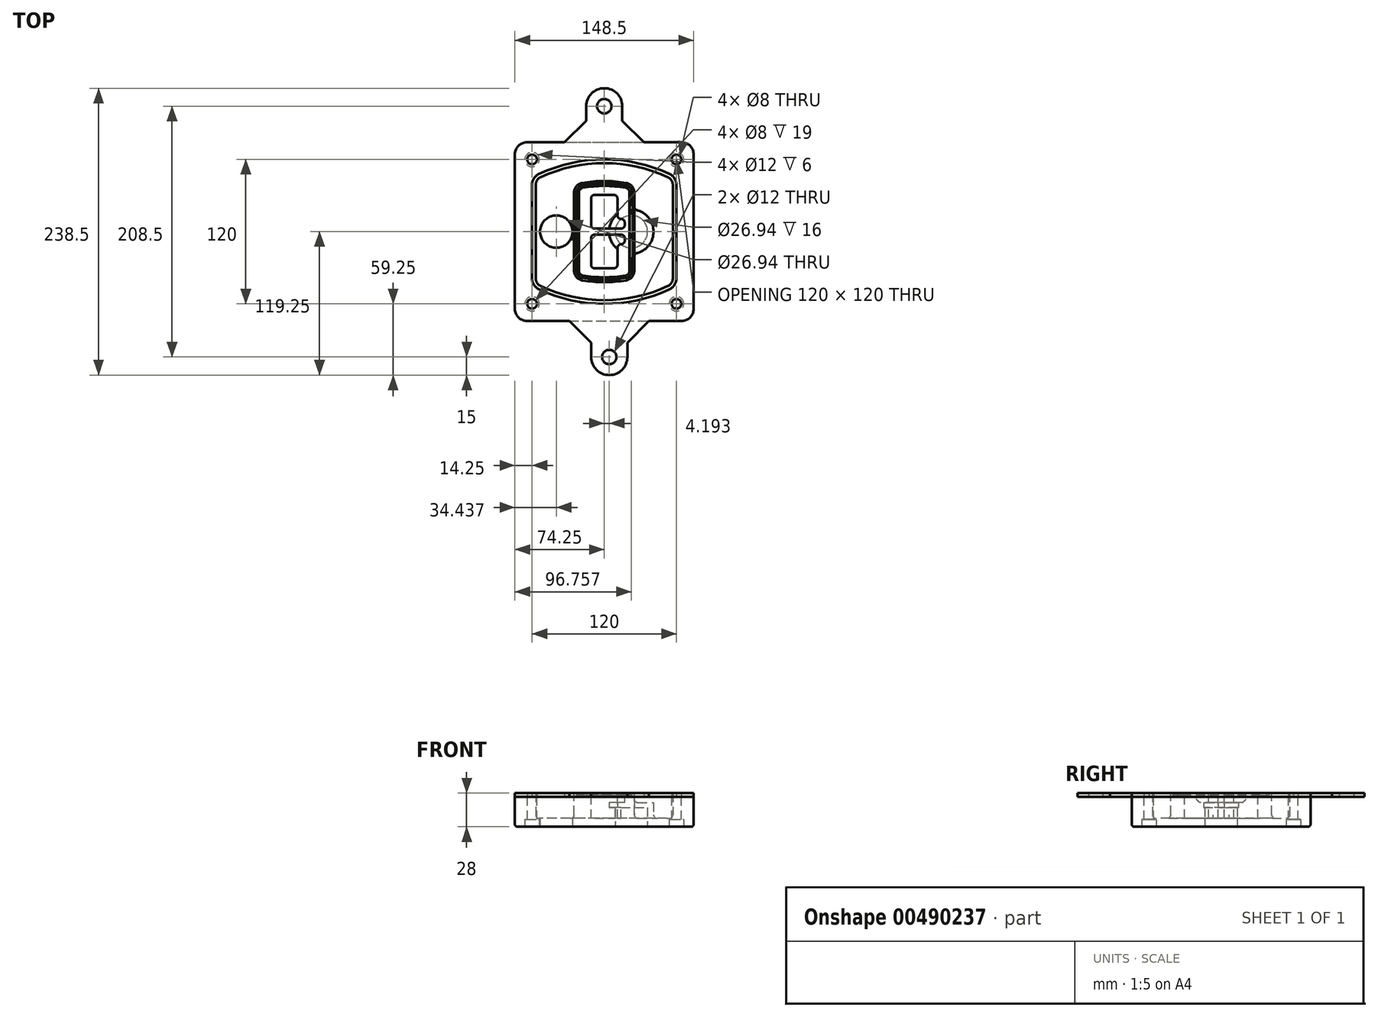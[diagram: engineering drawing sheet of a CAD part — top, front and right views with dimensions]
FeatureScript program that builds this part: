
annotation { "Feature Type Name" : "Feature", "Feature Type Description" : "" }
export const myFeature = defineFeature(function(context is Context, id is Id, definition is map)
    precondition{}
    {
        {
            var Q0;
            Q0=qCreatedBy(makeId("Top.planeOp"),FACE);
            var sketch = newSketch(context, id + "F0", { "sketchPlane" : qUnion([Q0])});
            skPoint(sketch, "E0.rect.middle", {"position": v(0, 0) * mm});
            skLineSegment(sketch, "E1.bottom", {"start": v(-64.25, -74.25) * mm, "end": v(64.25, -74.25) * mm});
            skLineSegment(sketch, "E1.top", {"start": v(-64.25, 74.25) * mm, "end": v(64.25, 74.25) * mm});
            skLineSegment(sketch, "E1.left", {"start": v(-74.25, -64.25) * mm, "end": v(-74.25, 64.25) * mm});
            skLineSegment(sketch, "E1.right", {"start": v(74.25, -64.25) * mm, "end": v(74.25, 64.25) * mm});
            skLineSegment(sketch, "E2", {"start": v(-74.25, 74.25) * mm, "end": v(74.25, -74.25) * mm, "construction": true});
            skLineSegment(sketch, "E3", {"start": v(74.25, 74.25) * mm, "end": v(-74.25, -74.25) * mm, "construction": true});
            skCircle(sketch, "E4", {"center": v(-60, 60) * mm, "radius": 4 * mm});
            skCircle(sketch, "E5", {"center": v(60, 60) * mm, "radius": 4 * mm});
            skCircle(sketch, "E6", {"center": v(60, -60) * mm, "radius": 4 * mm});
            skCircle(sketch, "E7", {"center": v(-60, -60) * mm, "radius": 4 * mm});
            skLineSegment(sketch, "E8", {"start": v(-60, 60) * mm, "end": v(60, 60) * mm, "construction": true});
            skLineSegment(sketch, "E9", {"start": v(60, 60) * mm, "end": v(60, -60) * mm, "construction": true});
            skLineSegment(sketch, "E10", {"start": v(60, -60) * mm, "end": v(-60, -60) * mm, "construction": true});
            skLineSegment(sketch, "E11", {"start": v(-60, -60) * mm, "end": v(-60, 60) * mm, "construction": true});
            skLineSegment(sketch, "E12", {"start": v(-60, 38.83) * mm, "end": v(-60, -38.83) * mm});
            skLineSegment(sketch, "E13", {"start": v(60, 38.83) * mm, "end": v(60, -38.83) * mm});
            skArc(sketch, "E14", {"start": v(54.26, 47.88) * mm, "mid": v(0, 60) * mm, "end": v(-54.26, 47.88) * mm});
            skArc(sketch, "E15", {"start": v(-54.26, -47.88) * mm, "mid": v(0, -60) * mm, "end": v(54.26, -47.88) * mm});
            skLineSegment(sketch, "E16", {"start": v(-60, 0) * mm, "end": v(60, 0) * mm, "construction": true});
            skPoint(sketch, "E17.visualSharp", {"position": v(-60, -45) * mm});
            skArc(sketch, "E17.filletArc", {"start": v(-60, -38.83) * mm, "mid": v(-58.44, -44.2) * mm, "end": v(-54.26, -47.88) * mm});
            skPoint(sketch, "E18.visualSharp", {"position": v(-60, 45) * mm});
            skArc(sketch, "E18.filletArc", {"start": v(-54.26, 47.88) * mm, "mid": v(-58.44, 44.2) * mm, "end": v(-60, 38.83) * mm});
            skPoint(sketch, "E19.visualSharp", {"position": v(60, 45) * mm});
            skArc(sketch, "E19.filletArc", {"start": v(60, 38.83) * mm, "mid": v(58.44, 44.2) * mm, "end": v(54.26, 47.88) * mm});
            skPoint(sketch, "E20.visualSharp", {"position": v(60, -45) * mm});
            skArc(sketch, "E20.filletArc", {"start": v(54.26, -47.88) * mm, "mid": v(58.44, -44.2) * mm, "end": v(60, -38.83) * mm});
            skPoint(sketch, "E21.visualSharp", {"position": v(-74.25, 74.25) * mm});
            skArc(sketch, "E21.filletArc", {"start": v(-64.25, 74.25) * mm, "mid": v(-71.32, 71.32) * mm, "end": v(-74.25, 64.25) * mm});
            skPoint(sketch, "E22.visualSharp", {"position": v(74.25, 74.25) * mm});
            skArc(sketch, "E22.filletArc", {"start": v(74.25, 64.25) * mm, "mid": v(71.32, 71.32) * mm, "end": v(64.25, 74.25) * mm});
            skPoint(sketch, "E23.visualSharp", {"position": v(74.25, -74.25) * mm});
            skArc(sketch, "E23.filletArc", {"start": v(64.25, -74.25) * mm, "mid": v(71.32, -71.32) * mm, "end": v(74.25, -64.25) * mm});
            skPoint(sketch, "E24.visualSharp", {"position": v(-74.25, -74.25) * mm});
            skArc(sketch, "E24.filletArc", {"start": v(-74.25, -64.25) * mm, "mid": v(-71.32, -71.32) * mm, "end": v(-64.25, -74.25) * mm});
            skArc(sketch, "E25.0", {"start": v(57, 38.83) * mm, "mid": v(55.9, 42.58) * mm, "end": v(52.98, 45.17) * mm});
            skLineSegment(sketch, "E25.1", {"start": v(57, 38.83) * mm, "end": v(57, -38.83) * mm});
            skArc(sketch, "E25.2", {"start": v(52.98, -45.17) * mm, "mid": v(55.9, -42.58) * mm, "end": v(57, -38.83) * mm});
            skArc(sketch, "E25.3", {"start": v(-52.98, -45.17) * mm, "mid": v(0, -57) * mm, "end": v(52.98, -45.17) * mm});
            skArc(sketch, "E25.4", {"start": v(-57, -38.83) * mm, "mid": v(-55.9, -42.58) * mm, "end": v(-52.98, -45.17) * mm});
            skArc(sketch, "E25.5", {"start": v(52.98, 45.17) * mm, "mid": v(0, 57) * mm, "end": v(-52.98, 45.17) * mm});
            skLineSegment(sketch, "E25.6", {"start": v(-57, 38.83) * mm, "end": v(-57, -38.83) * mm});
            skArc(sketch, "E25.7", {"start": v(-52.98, 45.17) * mm, "mid": v(-55.9, 42.58) * mm, "end": v(-57, 38.83) * mm});
            skArc(sketch, "E26.0", {"start": v(-55.96, 51.5) * mm, "mid": v(-61.82, 46.33) * mm, "end": v(-64, 38.83) * mm});
            skArc(sketch, "E26.1", {"start": v(55.96, 51.5) * mm, "mid": v(0, 64) * mm, "end": v(-55.96, 51.5) * mm});
            skArc(sketch, "E26.2", {"start": v(64, 38.83) * mm, "mid": v(61.82, 46.33) * mm, "end": v(55.96, 51.5) * mm});
            skLineSegment(sketch, "E26.3", {"start": v(64, 38.83) * mm, "end": v(64, -38.83) * mm});
            skArc(sketch, "E26.4", {"start": v(55.96, -51.5) * mm, "mid": v(61.82, -46.33) * mm, "end": v(64, -38.83) * mm});
            skLineSegment(sketch, "E26.5", {"start": v(-64, 38.83) * mm, "end": v(-64, -38.83) * mm});
            skArc(sketch, "E26.6", {"start": v(-55.96, -51.5) * mm, "mid": v(0, -64) * mm, "end": v(55.96, -51.5) * mm});
            skArc(sketch, "E26.7", {"start": v(-64, -38.83) * mm, "mid": v(-61.82, -46.33) * mm, "end": v(-55.96, -51.5) * mm});
            skSolve(sketch);
        }
        {
            var Q0;
            Q0=makeQuery(id+"F0.imprint","IMPRINT",FACE,{"disambiguationData":[TD([[makeQuery(id+"F0.imprint","IMPRINT",EDGE,{"derivedFrom":sQuery(id+"F0.wireOp",EDGE,"E1.bottom")}),1.0]])]});
            var Q1;
            Q1=makeQuery(id+"F0.imprint","IMPRINT",FACE,{"disambiguationData":[TD([[makeQuery(id+"F0.imprint","IMPRINT",EDGE,{"derivedFrom":sQuery(id+"F0.wireOp",EDGE,"E12")}),1.0]])]});
            var Q2;
            Q2=makeQuery(id+"F0.imprint","IMPRINT",FACE,{"disambiguationData":[TD([[makeQuery(id+"F0.imprint","IMPRINT",EDGE,{"derivedFrom":sQuery(id+"F0.wireOp",EDGE,"E25.0")}),1.0]])]});
            var Q3;
            Q3=makeQuery(id+"F0.imprint","IMPRINT",FACE,{"disambiguationData":[TD([[makeQuery(id+"F0.imprint","IMPRINT",EDGE,{"derivedFrom":sQuery(id+"F0.wireOp",EDGE,"E12")}),-1.0]])]});
            extrude(context, id + "F1", {"entities" : qUnion([Q0, Q1, Q2, Q3]), "oppositeDirection" : true, "depth" : 25 * mm});
        }
        {
            var Q0;
            Q0=makeQuery(id+"F0.imprint","IMPRINT",FACE,{"disambiguationData":[TD([[makeQuery(id+"F0.imprint","IMPRINT",EDGE,{"derivedFrom":sQuery(id+"F0.wireOp",EDGE,"E12")}),1.0]])]});
            extrude(context, id + "F2", {"entities" : qUnion([Q0]), "operationType" : NewBodyOperationType.ADD, "depth" : 3 * mm});
        }
        {
            var Q0;
            Q0=makeQuery(id+"F0.imprint","IMPRINT",FACE,{"disambiguationData":[TD([[makeQuery(id+"F0.imprint","IMPRINT",EDGE,{"derivedFrom":sQuery(id+"F0.wireOp",EDGE,"E25.0")}),1.0]])]});
            extrude(context, id + "F3", {"entities" : qUnion([Q0]), "operationType" : NewBodyOperationType.REMOVE, "oppositeDirection" : true, "depth" : 18 * mm});
        }
        {
            var Q0;
            Q0=makeQuery(id+"F2.opExtrude","CAP_FACE",FACE,{"disambiguationData":[OSD([sQuery(id+"F0.wireOp",EDGE,"E12"),sQuery(id+"F0.wireOp",EDGE,"E13"),sQuery(id+"F0.wireOp",EDGE,"E14"),sQuery(id+"F0.wireOp",EDGE,"E15"),sQuery(id+"F0.wireOp",EDGE,"E17.filletArc"),sQuery(id+"F0.wireOp",EDGE,"E18.filletArc"),sQuery(id+"F0.wireOp",EDGE,"E19.filletArc"),sQuery(id+"F0.wireOp",EDGE,"E20.filletArc"),sQuery(id+"F0.wireOp",EDGE,"E25.0"),sQuery(id+"F0.wireOp",EDGE,"E25.1"),sQuery(id+"F0.wireOp",EDGE,"E25.2"),sQuery(id+"F0.wireOp",EDGE,"E25.3"),sQuery(id+"F0.wireOp",EDGE,"E25.4"),sQuery(id+"F0.wireOp",EDGE,"E25.5"),sQuery(id+"F0.wireOp",EDGE,"E25.6"),sQuery(id+"F0.wireOp",EDGE,"E25.7")])],"isStart":false});
            var sketch = newSketch(context, id + "F4", { "sketchPlane" : qUnion([Q0])});
            skArc(sketch, "E27.0", {"start": v(-18.34, -40.45) * mm, "mid": v(0, -42) * mm, "end": v(18.34, -40.45) * mm});
            skArc(sketch, "E28.0", {"start": v(18.34, 40.45) * mm, "mid": v(0, 42) * mm, "end": v(-18.34, 40.45) * mm});
            skLineSegment(sketch, "E29", {"start": v(-25, 32.57) * mm, "end": v(-25, -32.57) * mm});
            skLineSegment(sketch, "E30", {"start": v(25, 32.57) * mm, "end": v(25, -32.57) * mm});
            skLineSegment(sketch, "E31", {"start": v(-25, 39.1) * mm, "end": v(25, 39.1) * mm, "construction": true});
            skLineSegment(sketch, "E32", {"start": v(-25, -39.1) * mm, "end": v(25, -39.1) * mm, "construction": true});
            skPoint(sketch, "E33.visualSharp", {"position": v(-25, 39.1) * mm});
            skArc(sketch, "E33.filletArc", {"start": v(-18.34, 40.45) * mm, "mid": v(-23.11, 37.73) * mm, "end": v(-25, 32.57) * mm});
            skPoint(sketch, "E34.visualSharp", {"position": v(25, 39.1) * mm});
            skArc(sketch, "E34.filletArc", {"start": v(25, 32.57) * mm, "mid": v(23.11, 37.73) * mm, "end": v(18.34, 40.45) * mm});
            skPoint(sketch, "E35.visualSharp", {"position": v(25, -39.1) * mm});
            skArc(sketch, "E35.filletArc", {"start": v(18.34, -40.45) * mm, "mid": v(23.11, -37.73) * mm, "end": v(25, -32.57) * mm});
            skPoint(sketch, "E36.visualSharp", {"position": v(-25, -39.1) * mm});
            skArc(sketch, "E36.filletArc", {"start": v(-25, -32.57) * mm, "mid": v(-23.11, -37.73) * mm, "end": v(-18.34, -40.45) * mm});
            skArc(sketch, "E37.0", {"start": v(52.98, 45.17) * mm, "mid": v(0, 57) * mm, "end": v(-52.98, 45.17) * mm});
            skArc(sketch, "E37.1", {"start": v(-52.98, 45.17) * mm, "mid": v(-55.9, 42.58) * mm, "end": v(-57, 38.83) * mm});
            skLineSegment(sketch, "E37.2", {"start": v(-57, 38.83) * mm, "end": v(-57, -38.83) * mm});
            skArc(sketch, "E37.3", {"start": v(-57, -38.83) * mm, "mid": v(-55.9, -42.58) * mm, "end": v(-52.98, -45.17) * mm});
            skArc(sketch, "E37.4", {"start": v(-52.98, -45.17) * mm, "mid": v(0, -57) * mm, "end": v(52.98, -45.17) * mm});
            skArc(sketch, "E37.5", {"start": v(52.98, -45.17) * mm, "mid": v(55.9, -42.58) * mm, "end": v(57, -38.83) * mm});
            skLineSegment(sketch, "E37.6", {"start": v(57, 38.83) * mm, "end": v(57, -38.83) * mm});
            skArc(sketch, "E37.7", {"start": v(57, 38.83) * mm, "mid": v(55.9, 42.58) * mm, "end": v(52.98, 45.17) * mm});
            skLineSegment(sketch, "E38.0", {"start": v(23, 32.57) * mm, "end": v(23, -32.57) * mm});
            skArc(sketch, "E38.1", {"start": v(18, -38.48) * mm, "mid": v(21.58, -36.44) * mm, "end": v(23, -32.57) * mm});
            skArc(sketch, "E38.2", {"start": v(-18, -38.48) * mm, "mid": v(0, -40) * mm, "end": v(18, -38.48) * mm});
            skArc(sketch, "E38.3", {"start": v(-23, -32.57) * mm, "mid": v(-21.58, -36.44) * mm, "end": v(-18, -38.48) * mm});
            skLineSegment(sketch, "E38.4", {"start": v(-23, 32.57) * mm, "end": v(-23, -32.57) * mm});
            skArc(sketch, "E38.5", {"start": v(23, 32.57) * mm, "mid": v(21.58, 36.44) * mm, "end": v(18, 38.48) * mm});
            skArc(sketch, "E38.6", {"start": v(-18, 38.48) * mm, "mid": v(-21.58, 36.44) * mm, "end": v(-23, 32.57) * mm});
            skArc(sketch, "E38.7", {"start": v(18, 38.48) * mm, "mid": v(0, 40) * mm, "end": v(-18, 38.48) * mm});
            skArc(sketch, "E39.0", {"start": v(21, 32.57) * mm, "mid": v(20.06, 35.15) * mm, "end": v(17.67, 36.5) * mm});
            skLineSegment(sketch, "E39.1", {"start": v(21, 32.57) * mm, "end": v(21, -32.57) * mm});
            skArc(sketch, "E39.2", {"start": v(17.67, -36.5) * mm, "mid": v(20.06, -35.15) * mm, "end": v(21, -32.57) * mm});
            skArc(sketch, "E39.3", {"start": v(-17.67, -36.5) * mm, "mid": v(0, -38) * mm, "end": v(17.67, -36.5) * mm});
            skArc(sketch, "E39.4", {"start": v(-21, -32.57) * mm, "mid": v(-20.06, -35.15) * mm, "end": v(-17.67, -36.5) * mm});
            skArc(sketch, "E39.5", {"start": v(17.67, 36.5) * mm, "mid": v(0, 38) * mm, "end": v(-17.67, 36.5) * mm});
            skLineSegment(sketch, "E39.6", {"start": v(-21, 32.57) * mm, "end": v(-21, -32.57) * mm});
            skArc(sketch, "E39.7", {"start": v(-17.67, 36.5) * mm, "mid": v(-20.06, 35.15) * mm, "end": v(-21, 32.57) * mm});
            skLineSegment(sketch, "E40", {"start": v(-25, 0) * mm, "end": v(25, 0) * mm, "construction": true});
            skLineSegment(sketch, "E41", {"start": v(-11, 5.5) * mm, "end": v(-11, 27.5) * mm});
            skLineSegment(sketch, "E42", {"start": v(-8, 30.5) * mm, "end": v(8, 30.5) * mm});
            skLineSegment(sketch, "E43", {"start": v(11, 27.5) * mm, "end": v(11, 13.5) * mm});
            skLineSegment(sketch, "E44", {"start": v(14, 10.5) * mm, "end": v(14, 10.5) * mm});
            skLineSegment(sketch, "E45", {"start": v(17, 7.5) * mm, "end": v(17, 5.5) * mm});
            skLineSegment(sketch, "E46", {"start": v(14, 2.5) * mm, "end": v(-8, 2.5) * mm});
            skPoint(sketch, "E47.visualSharp", {"position": v(-11, 30.5) * mm});
            skArc(sketch, "E47.filletArc", {"start": v(-8, 30.5) * mm, "mid": v(-10.12, 29.62) * mm, "end": v(-11, 27.5) * mm});
            skPoint(sketch, "E48.visualSharp", {"position": v(11, 30.5) * mm});
            skArc(sketch, "E48.filletArc", {"start": v(11, 27.5) * mm, "mid": v(10.12, 29.62) * mm, "end": v(8, 30.5) * mm});
            skPoint(sketch, "E49.visualSharp", {"position": v(11, 10.5) * mm});
            skArc(sketch, "E49.filletArc", {"start": v(11, 13.5) * mm, "mid": v(11.88, 11.38) * mm, "end": v(14, 10.5) * mm});
            skPoint(sketch, "E50.visualSharp", {"position": v(17, 10.5) * mm});
            skArc(sketch, "E50.filletArc", {"start": v(17, 7.5) * mm, "mid": v(16.12, 9.62) * mm, "end": v(14, 10.5) * mm});
            skPoint(sketch, "E51.visualSharp", {"position": v(17, 2.5) * mm});
            skArc(sketch, "E51.filletArc", {"start": v(14, 2.5) * mm, "mid": v(16.12, 3.38) * mm, "end": v(17, 5.5) * mm});
            skPoint(sketch, "E52.visualSharp", {"position": v(-11, 2.5) * mm});
            skArc(sketch, "E52.filletArc", {"start": v(-11, 5.5) * mm, "mid": v(-10.12, 3.38) * mm, "end": v(-8, 2.5) * mm});
            skLineSegment(sketch, "E53.0.MirrorCS", {"start": v(14, -2.5) * mm, "end": v(-8, -2.5) * mm});
            skArc(sketch, "E54.0.MirrorCS", {"start": v(-11, -5.5) * mm, "mid": v(-10.12, -3.38) * mm, "end": v(-8, -2.5) * mm});
            skLineSegment(sketch, "E55.0.MirrorCS", {"start": v(-11, -5.5) * mm, "end": v(-11, -27.5) * mm});
            skArc(sketch, "E56.0.MirrorCS", {"start": v(-8, -30.5) * mm, "mid": v(-10.12, -29.62) * mm, "end": v(-11, -27.5) * mm});
            skLineSegment(sketch, "E57.0.MirrorCS", {"start": v(-8, -30.5) * mm, "end": v(8, -30.5) * mm});
            skArc(sketch, "E58.0.MirrorCS", {"start": v(11, -27.5) * mm, "mid": v(10.12, -29.62) * mm, "end": v(8, -30.5) * mm});
            skLineSegment(sketch, "E59.0.MirrorCS", {"start": v(11, -27.5) * mm, "end": v(11, -13.5) * mm});
            skArc(sketch, "E60.0.MirrorCS", {"start": v(11, -13.5) * mm, "mid": v(11.88, -11.38) * mm, "end": v(14, -10.5) * mm});
            skArc(sketch, "E61.0.MirrorCS", {"start": v(17, -7.5) * mm, "mid": v(16.12, -9.62) * mm, "end": v(14, -10.5) * mm});
            skLineSegment(sketch, "E62.0.MirrorCS", {"start": v(17, -7.5) * mm, "end": v(17, -5.5) * mm});
            skArc(sketch, "E63.0.MirrorCS", {"start": v(14, -2.5) * mm, "mid": v(16.12, -3.38) * mm, "end": v(17, -5.5) * mm});
            skSolve(sketch);
        }
        {
            var Q0;
            Q0=makeQuery(id+"F4.imprint","IMPRINT",FACE,{"disambiguationData":[TD([[makeQuery(id+"F4.imprint","IMPRINT",EDGE,{"derivedFrom":sQuery(id+"F4.wireOp",EDGE,"E27.0")}),1.0]])]});
            var Q1;
            Q1=makeQuery(id+"F4.imprint","IMPRINT",FACE,{"disambiguationData":[TD([[makeQuery(id+"F4.imprint","IMPRINT",EDGE,{"derivedFrom":sQuery(id+"F4.wireOp",EDGE,"E38.0")}),-1.0]])]});
            var Q2;
            Q2=makeQuery(id+"F4.imprint","IMPRINT",FACE,{"disambiguationData":[TD([[makeQuery(id+"F4.imprint","IMPRINT",EDGE,{"derivedFrom":sQuery(id+"F4.wireOp",EDGE,"E39.0")}),1.0]])]});
            extrude(context, id + "F5", {"entities" : qUnion([Q0, Q1, Q2]), "operationType" : NewBodyOperationType.ADD, "endBound" : BoundingType.UP_TO_NEXT, "oppositeDirection" : true, "depth" : 25 * mm});
        }
        {
            var Q0;
            Q0=makeQuery(id+"F4.imprint","IMPRINT",FACE,{"disambiguationData":[TD([[makeQuery(id+"F4.imprint","IMPRINT",EDGE,{"derivedFrom":sQuery(id+"F4.wireOp",EDGE,"E38.0")}),-1.0]])]});
            extrude(context, id + "F6", {"entities" : qUnion([Q0]), "operationType" : NewBodyOperationType.REMOVE, "oppositeDirection" : true, "depth" : 2 * mm});
        }
        {
            var Q0;
            Q0=makeQuery(id+"F1.opExtrude","CAP_FACE",FACE,{"disambiguationData":[OSD([sQuery(id+"F0.wireOp",EDGE,"E1.bottom"),sQuery(id+"F0.wireOp",EDGE,"E1.top"),sQuery(id+"F0.wireOp",EDGE,"E1.left"),sQuery(id+"F0.wireOp",EDGE,"E1.right"),sQuery(id+"F0.wireOp",EDGE,"E4"),sQuery(id+"F0.wireOp",EDGE,"E5"),sQuery(id+"F0.wireOp",EDGE,"E6"),sQuery(id+"F0.wireOp",EDGE,"E7"),sQuery(id+"F0.wireOp",EDGE,"E21.filletArc"),sQuery(id+"F0.wireOp",EDGE,"E22.filletArc"),sQuery(id+"F0.wireOp",EDGE,"E23.filletArc"),sQuery(id+"F0.wireOp",EDGE,"E24.filletArc")])],"isStart":false});
            var sketch = newSketch(context, id + "F7", { "sketchPlane" : qUnion([Q0])});
            skCircle(sketch, "E64", {"center": v(22.5, 0) * mm, "radius": 13.47 * mm});
            skCircle(sketch, "E65", {"center": v(-39.81, 0) * mm, "radius": 13.47 * mm});
            skLineSegment(sketch, "E66", {"start": v(74.25, 0) * mm, "end": v(-74.25, 0) * mm});
            skCircle(sketch, "E67", {"center": v(22.5, 0) * mm, "radius": 18.47 * mm});
            skCircle(sketch, "E68", {"center": v(60, -60) * mm, "radius": 6 * mm});
            skCircle(sketch, "E69", {"center": v(-60, -60) * mm, "radius": 6 * mm});
            skCircle(sketch, "E70", {"center": v(-60, 60) * mm, "radius": 6 * mm});
            skCircle(sketch, "E71", {"center": v(60, 60) * mm, "radius": 6 * mm});
            skSolve(sketch);
        }
        {
            var Q0;
            {var subQ1=sQuery(id+"F7.wireOp",EDGE,"E66");var subQ4=sQuery(id+"F7.wireOp",EDGE,"E64");var subQ6=makeQuery(id+"F7.imprint","INTERSECT",VERTEX,{"disambiguationData":[OD(0.0)],"derivedFrom":[subQ4,subQ1]});Q0=makeQuery(id+"F7.imprint","IMPRINT",FACE,{"disambiguationData":[TD([[makeQuery(id+"F7.imprint","IMPRINT",EDGE,{"disambiguationData":[TD([[subQ6,-1.0]])],"derivedFrom":subQ4}),-1.0]])]});}
            var Q1;
            {var subQ0=sQuery(id+"F7.wireOp",EDGE,"E66");var subQ1=sQuery(id+"F7.wireOp",EDGE,"E64");var subQ3=makeQuery(id+"F7.imprint","INTERSECT",VERTEX,{"disambiguationData":[OD(0.0)],"derivedFrom":[subQ1,subQ0]});Q1=makeQuery(id+"F7.imprint","IMPRINT",FACE,{"disambiguationData":[TD([[makeQuery(id+"F7.imprint","IMPRINT",EDGE,{"disambiguationData":[TD([[subQ3,-1.0]])],"derivedFrom":subQ1}),1.0]])]});}
            var Q2;
            {var subQ0=sQuery(id+"F7.wireOp",EDGE,"E66");var subQ1=sQuery(id+"F7.wireOp",EDGE,"E64");var subQ3=makeQuery(id+"F7.imprint","INTERSECT",VERTEX,{"disambiguationData":[OD(0.0)],"derivedFrom":[subQ1,subQ0]});Q2=makeQuery(id+"F7.imprint","IMPRINT",FACE,{"disambiguationData":[TD([[makeQuery(id+"F7.imprint","IMPRINT",EDGE,{"disambiguationData":[TD([[subQ3,1.0]])],"derivedFrom":subQ1}),1.0]])]});}
            var Q3;
            {var subQ1=sQuery(id+"F7.wireOp",EDGE,"E66");var subQ4=sQuery(id+"F7.wireOp",EDGE,"E64");var subQ6=makeQuery(id+"F7.imprint","INTERSECT",VERTEX,{"disambiguationData":[OD(0.0)],"derivedFrom":[subQ4,subQ1]});Q3=makeQuery(id+"F7.imprint","IMPRINT",FACE,{"disambiguationData":[TD([[makeQuery(id+"F7.imprint","IMPRINT",EDGE,{"disambiguationData":[TD([[subQ6,1.0]])],"derivedFrom":subQ4}),-1.0]])]});}
            extrude(context, id + "F8", {"entities" : qUnion([Q0, Q1, Q2, Q3]), "operationType" : NewBodyOperationType.ADD, "oppositeDirection" : true, "depth" : 20 * mm});
        }
        {
            var Q0;
            {var subQ0=sQuery(id+"F7.wireOp",EDGE,"E66");var subQ1=sQuery(id+"F7.wireOp",EDGE,"E64");var subQ3=makeQuery(id+"F7.imprint","INTERSECT",VERTEX,{"disambiguationData":[OD(0.0)],"derivedFrom":[subQ1,subQ0]});Q0=makeQuery(id+"F7.imprint","IMPRINT",FACE,{"disambiguationData":[TD([[makeQuery(id+"F7.imprint","IMPRINT",EDGE,{"disambiguationData":[TD([[subQ3,-1.0]])],"derivedFrom":subQ1}),1.0]])]});}
            var Q1;
            {var subQ0=sQuery(id+"F7.wireOp",EDGE,"E66");var subQ1=sQuery(id+"F7.wireOp",EDGE,"E64");var subQ3=makeQuery(id+"F7.imprint","INTERSECT",VERTEX,{"disambiguationData":[OD(0.0)],"derivedFrom":[subQ1,subQ0]});Q1=makeQuery(id+"F7.imprint","IMPRINT",FACE,{"disambiguationData":[TD([[makeQuery(id+"F7.imprint","IMPRINT",EDGE,{"disambiguationData":[TD([[subQ3,1.0]])],"derivedFrom":subQ1}),1.0]])]});}
            extrude(context, id + "F9", {"entities" : qUnion([Q0, Q1]), "operationType" : NewBodyOperationType.REMOVE, "oppositeDirection" : true, "depth" : 16 * mm});
        }
        {
            var Q0;
            {var subQ0=sQuery(id+"F7.wireOp",EDGE,"E66");var subQ1=sQuery(id+"F7.wireOp",EDGE,"E65");var subQ3=makeQuery(id+"F7.imprint","INTERSECT",VERTEX,{"disambiguationData":[OD(0.0)],"derivedFrom":[subQ1,subQ0]});Q0=makeQuery(id+"F7.imprint","IMPRINT",FACE,{"disambiguationData":[TD([[makeQuery(id+"F7.imprint","IMPRINT",EDGE,{"disambiguationData":[TD([[subQ3,-1.0]])],"derivedFrom":subQ1}),1.0]])]});}
            var Q1;
            {var subQ0=sQuery(id+"F7.wireOp",EDGE,"E66");var subQ1=sQuery(id+"F7.wireOp",EDGE,"E65");var subQ3=makeQuery(id+"F7.imprint","INTERSECT",VERTEX,{"disambiguationData":[OD(0.0)],"derivedFrom":[subQ1,subQ0]});Q1=makeQuery(id+"F7.imprint","IMPRINT",FACE,{"disambiguationData":[TD([[makeQuery(id+"F7.imprint","IMPRINT",EDGE,{"disambiguationData":[TD([[subQ3,1.0]])],"derivedFrom":subQ1}),1.0]])]});}
            extrude(context, id + "F10", {"entities" : qUnion([Q0, Q1]), "operationType" : NewBodyOperationType.REMOVE, "oppositeDirection" : true, "depth" : 25 * mm});
        }
        {
            var Q0;
            Q0=makeQuery(id+"F7.imprint","IMPRINT",FACE,{"disambiguationData":[TD([[makeQuery(id+"F7.imprint","IMPRINT",EDGE,{"derivedFrom":sQuery(id+"F7.wireOp",EDGE,"E68")}),1.0]])]});
            var Q1;
            Q1=makeQuery(id+"F7.imprint","IMPRINT",FACE,{"disambiguationData":[TD([[makeQuery(id+"F7.imprint","IMPRINT",EDGE,{"derivedFrom":makeQuery(id+"F1.opExtrude","CAP_EDGE",EDGE,{"disambiguationData":[OSD([sQuery(id+"F0.wireOp",EDGE,"E5")])],"isStart":false})}),-1.0]])]});
            var Q2;
            Q2=makeQuery(id+"F7.imprint","IMPRINT",FACE,{"disambiguationData":[TD([[makeQuery(id+"F7.imprint","IMPRINT",EDGE,{"derivedFrom":sQuery(id+"F7.wireOp",EDGE,"E69")}),1.0]])]});
            var Q3;
            Q3=makeQuery(id+"F7.imprint","IMPRINT",FACE,{"disambiguationData":[TD([[makeQuery(id+"F7.imprint","IMPRINT",EDGE,{"derivedFrom":makeQuery(id+"F1.opExtrude","CAP_EDGE",EDGE,{"disambiguationData":[OSD([sQuery(id+"F0.wireOp",EDGE,"E4")])],"isStart":false})}),-1.0]])]});
            var Q4;
            Q4=makeQuery(id+"F7.imprint","IMPRINT",FACE,{"disambiguationData":[TD([[makeQuery(id+"F7.imprint","IMPRINT",EDGE,{"derivedFrom":sQuery(id+"F7.wireOp",EDGE,"E70")}),1.0]])]});
            var Q5;
            Q5=makeQuery(id+"F7.imprint","IMPRINT",FACE,{"disambiguationData":[TD([[makeQuery(id+"F7.imprint","IMPRINT",EDGE,{"derivedFrom":makeQuery(id+"F1.opExtrude","CAP_EDGE",EDGE,{"disambiguationData":[OSD([sQuery(id+"F0.wireOp",EDGE,"E7")])],"isStart":false})}),-1.0]])]});
            var Q6;
            Q6=makeQuery(id+"F7.imprint","IMPRINT",FACE,{"disambiguationData":[TD([[makeQuery(id+"F7.imprint","IMPRINT",EDGE,{"derivedFrom":sQuery(id+"F7.wireOp",EDGE,"E71")}),1.0]])]});
            var Q7;
            Q7=makeQuery(id+"F7.imprint","IMPRINT",FACE,{"disambiguationData":[TD([[makeQuery(id+"F7.imprint","IMPRINT",EDGE,{"derivedFrom":makeQuery(id+"F1.opExtrude","CAP_EDGE",EDGE,{"disambiguationData":[OSD([sQuery(id+"F0.wireOp",EDGE,"E6")])],"isStart":false})}),-1.0]])]});
            extrude(context, id + "F11", {"entities" : qUnion([Q0, Q1, Q2, Q3, Q4, Q5, Q6, Q7]), "operationType" : NewBodyOperationType.REMOVE, "oppositeDirection" : true, "depth" : 6 * mm});
        }
        {
            var Q0;
            Q0=makeQuery(id+"F9.boolean.opBoolean","COPY",FACE,{"derivedFrom":makeQuery(id+"F9.opExtrude","CAP_FACE",FACE,{"disambiguationData":[OSD([sQuery(id+"F7.wireOp",EDGE,"E64")])],"isStart":false})});
            var sketch = newSketch(context, id + "F12", { "sketchPlane" : qUnion([Q0])});
            skArc(sketch, "E72.0", {"start": v(11, 14.45) * mm, "mid": v(6.45, 9.13) * mm, "end": v(4.2, 2.5) * mm});
            skArc(sketch, "E72.1", {"start": v(4.2, -2.5) * mm, "mid": v(6.45, -9.13) * mm, "end": v(11, -14.45) * mm});
            skLineSegment(sketch, "E73", {"start": v(4.2, -2.5) * mm, "end": v(14, -2.5) * mm});
            skLineSegment(sketch, "E74.0", {"start": v(14, 2.5) * mm, "end": v(4.2, 2.5) * mm});
            skArc(sketch, "E74.1", {"start": v(14, 2.5) * mm, "mid": v(16.12, 3.38) * mm, "end": v(17, 5.5) * mm});
            skLineSegment(sketch, "E74.2", {"start": v(17, 7.5) * mm, "end": v(17, 5.5) * mm});
            skArc(sketch, "E74.3", {"start": v(17, 7.5) * mm, "mid": v(16.12, 9.62) * mm, "end": v(14, 10.5) * mm});
            skArc(sketch, "E74.4", {"start": v(11, 13.5) * mm, "mid": v(11.88, 11.38) * mm, "end": v(14, 10.5) * mm});
            skLineSegment(sketch, "E74.5", {"start": v(11, 14.45) * mm, "end": v(11, 13.5) * mm});
            skLineSegment(sketch, "E74.7", {"start": v(14, -2.5) * mm, "end": v(4.2, -2.5) * mm});
            skArc(sketch, "E74.8", {"start": v(14, -2.5) * mm, "mid": v(16.12, -3.38) * mm, "end": v(17, -5.5) * mm});
            skLineSegment(sketch, "E74.9", {"start": v(17, -7.5) * mm, "end": v(17, -5.5) * mm});
            skArc(sketch, "E74.10", {"start": v(17, -7.5) * mm, "mid": v(16.12, -9.62) * mm, "end": v(14, -10.5) * mm});
            skArc(sketch, "E74.11", {"start": v(11, -13.5) * mm, "mid": v(11.88, -11.38) * mm, "end": v(14, -10.5) * mm});
            skLineSegment(sketch, "E74.12", {"start": v(11, -14.45) * mm, "end": v(11, -13.5) * mm});
            skPoint(sketch, "E75.orphan", {"position": v(11, -27.5) * mm});
            skPoint(sketch, "E76.orphan", {"position": v(-8, -2.5) * mm});
            skPoint(sketch, "E77.orphan", {"position": v(-8, 2.5) * mm});
            skPoint(sketch, "E78.orphan", {"position": v(11, 27.5) * mm});
            skSolve(sketch);
        }
        {
            var Q0;
            {var subQ7=sQuery(id+"F12.wireOp",EDGE,"E72.0");var subQ14=sQuery(id+"F12.wireOp",EDGE,"E72.1");var subQ16=sQuery(id+"F12.wireOp",EDGE,"E74.1");var subQ18=sQuery(id+"F12.wireOp",EDGE,"E74.8");Q0=qUnion([makeQuery(id+"F12.imprint","IMPRINT",FACE,{"disambiguationData":[TD([[makeQuery(id+"F12.imprint","IMPRINT",EDGE,{"derivedFrom":subQ7}),1.0]])]}),makeQuery(id+"F12.imprint","IMPRINT",FACE,{"disambiguationData":[TD([[makeQuery(id+"F12.imprint","IMPRINT",EDGE,{"derivedFrom":subQ14}),1.0]])]}),makeQuery(id+"F12.imprint","IMPRINT",FACE,{"disambiguationData":[TD([[makeQuery(id+"F12.imprint","IMPRINT",EDGE,{"derivedFrom":subQ16}),1.0]])]}),makeQuery(id+"F12.imprint","IMPRINT",FACE,{"disambiguationData":[TD([[makeQuery(id+"F12.imprint","IMPRINT",EDGE,{"derivedFrom":subQ18}),-1.0]])]})]);}
            var Q1;
            Q1=makeQuery(id+"F5.boolean.opBoolean","SPLIT",FACE,{"disambiguationData":[TD([makeQuery(id+"F5.opExtrude","SWEPT_FACE",FACE,{"disambiguationData":[OSD([sQuery(id+"F4.wireOp",EDGE,"E41")])]})])],"derivedFrom":makeQuery(id+"F3.boolean.opBoolean","COPY",FACE,{"derivedFrom":makeQuery(id+"F3.opExtrude","CAP_FACE",FACE,{"disambiguationData":[OSD([sQuery(id+"F0.wireOp",EDGE,"E25.0"),sQuery(id+"F0.wireOp",EDGE,"E25.1"),sQuery(id+"F0.wireOp",EDGE,"E25.2"),sQuery(id+"F0.wireOp",EDGE,"E25.3"),sQuery(id+"F0.wireOp",EDGE,"E25.4"),sQuery(id+"F0.wireOp",EDGE,"E25.5"),sQuery(id+"F0.wireOp",EDGE,"E25.6"),sQuery(id+"F0.wireOp",EDGE,"E25.7")])],"isStart":false})})});
            extrude(context, id + "F13", {"entities" : qUnion([Q0]), "operationType" : NewBodyOperationType.REMOVE, "endBound" : BoundingType.UP_TO_SURFACE, "endBoundEntityFace" : qUnion([Q1]), "depth" : 25 * mm});
        }
        {
            var Q0;
            Q0=makeQuery(id+"F3.boolean.opBoolean","COPY",EDGE,{"derivedFrom":makeQuery(id+"F3.opExtrude","CAP_EDGE",EDGE,{"disambiguationData":[OSD([sQuery(id+"F0.wireOp",EDGE,"E25.6")])],"isStart":false})});
            var Q1;
            Q1=makeQuery(id+"F8.boolean.opBoolean","INTERSECT",EDGE,{"derivedFrom":[makeQuery(id+"F5.opExtrude","SWEPT_FACE",FACE,{"disambiguationData":[OSD([sQuery(id+"F4.wireOp",EDGE,"E30")])]}),makeQuery(id+"F8.opExtrude","CAP_FACE",FACE,{"disambiguationData":[OSD([sQuery(id+"F7.wireOp",EDGE,"E67")])],"isStart":false})]});
            var Q2;
            Q2=makeQuery(id+"F8.boolean.opBoolean","INTERSECT",EDGE,{"disambiguationData":[OD(1.0)],"derivedFrom":[makeQuery(id+"F5.opExtrude","SWEPT_FACE",FACE,{"disambiguationData":[OSD([sQuery(id+"F4.wireOp",EDGE,"E30")])]}),makeQuery(id+"F8.opExtrude","SWEPT_FACE",FACE,{"disambiguationData":[OSD([sQuery(id+"F7.wireOp",EDGE,"E67")])]})]});
            var Q3;
            {var subQ0=sQuery(id+"F4.wireOp",EDGE,"E30");Q3=makeQuery(id+"F8.boolean.opBoolean","SPLIT",EDGE,{"disambiguationData":[TD([makeQuery(id+"F5.opExtrude","SWEPT_FACE",FACE,{"disambiguationData":[OSD([sQuery(id+"F4.wireOp",EDGE,"E35.filletArc")])]})])],"derivedFrom":makeQuery(id+"F5.opExtrude","CAP_EDGE",EDGE,{"disambiguationData":[OSD([subQ0])],"isStart":false})});}
            var Q4;
            {var subQ0=sQuery(id+"F0.wireOp",EDGE,"E25.7");var subQ1=sQuery(id+"F0.wireOp",EDGE,"E25.1");var subQ2=sQuery(id+"F0.wireOp",EDGE,"E25.6");var subQ3=sQuery(id+"F0.wireOp",EDGE,"E25.5");var subQ4=sQuery(id+"F0.wireOp",EDGE,"E25.4");var subQ5=sQuery(id+"F0.wireOp",EDGE,"E25.0");var subQ6=sQuery(id+"F0.wireOp",EDGE,"E25.2");var subQ7=sQuery(id+"F0.wireOp",EDGE,"E25.3");Q4=makeQuery(id+"F8.boolean.opBoolean","INTERSECT",EDGE,{"derivedFrom":[makeQuery(id+"F5.boolean.opBoolean","SPLIT",FACE,{"disambiguationData":[TD([makeQuery(id+"F2.opExtrude","SWEPT_FACE",FACE,{"disambiguationData":[OSD([subQ5])]})])],"derivedFrom":makeQuery(id+"F3.boolean.opBoolean","COPY",FACE,{"derivedFrom":makeQuery(id+"F3.opExtrude","CAP_FACE",FACE,{"disambiguationData":[OSD([subQ5,subQ1,subQ6,subQ7,subQ4,subQ3,subQ2,subQ0])],"isStart":false})})}),makeQuery(id+"F8.opExtrude","SWEPT_FACE",FACE,{"disambiguationData":[OSD([sQuery(id+"F7.wireOp",EDGE,"E67")])]})]});}
            var Q5;
            Q5=makeQuery(id+"F8.boolean.opBoolean","INTERSECT",EDGE,{"disambiguationData":[OD(0.0)],"derivedFrom":[makeQuery(id+"F5.opExtrude","SWEPT_FACE",FACE,{"disambiguationData":[OSD([sQuery(id+"F4.wireOp",EDGE,"E30")])]}),makeQuery(id+"F8.opExtrude","SWEPT_FACE",FACE,{"disambiguationData":[OSD([sQuery(id+"F7.wireOp",EDGE,"E67")])]})]});
            fillet(context, id + "F14", {"entities" : qUnion([Q0, Q1, Q2, Q3, Q4, Q5]), "radius" : 3 * mm, "tangentPropagation" : true, "allowEdgeOverflow" : false});
        }
        {
            var Q0;
            Q0=makeQuery(id+"F1.opExtrude","CAP_EDGE",EDGE,{"disambiguationData":[OSD([sQuery(id+"F0.wireOp",EDGE,"E1.bottom")])],"isStart":false});
            fillet(context, id + "F15", {"entities" : qUnion([Q0]), "radius" : 2 * mm, "tangentPropagation" : true, "allowEdgeOverflow" : false});
        }
        {
            var Q0;
            {var subQ0=sQuery(id+"F0.wireOp",EDGE,"E21.filletArc");var subQ1=sQuery(id+"F0.wireOp",EDGE,"E7");var subQ2=sQuery(id+"F0.wireOp",EDGE,"E6");var subQ3=sQuery(id+"F0.wireOp",EDGE,"E5");var subQ4=sQuery(id+"F0.wireOp",EDGE,"E4");var subQ5=sQuery(id+"F0.wireOp",EDGE,"E22.filletArc");var subQ6=sQuery(id+"F0.wireOp",EDGE,"E1.bottom");var subQ7=sQuery(id+"F0.wireOp",EDGE,"E1.right");var subQ8=sQuery(id+"F0.wireOp",EDGE,"E1.top");var subQ9=sQuery(id+"F0.wireOp",EDGE,"E1.left");var subQ10=sQuery(id+"F0.wireOp",EDGE,"E23.filletArc");var subQ11=sQuery(id+"F0.wireOp",EDGE,"E24.filletArc");Q0=makeQuery(id+"F2.boolean.opBoolean","SPLIT",FACE,{"disambiguationData":[TD([makeQuery(id+"F1.opExtrude","SWEPT_FACE",FACE,{"disambiguationData":[OSD([subQ6])]})])],"derivedFrom":makeQuery(id+"F1.opExtrude","CAP_FACE",FACE,{"disambiguationData":[OSD([subQ6,subQ8,subQ9,subQ7,subQ4,subQ3,subQ2,subQ1,subQ0,subQ5,subQ10,subQ11])],"isStart":true})});}
            var sketch = newSketch(context, id + "F16", { "sketchPlane" : qUnion([Q0])});
            skLineSegment(sketch, "E79", {"start": v(0, 74.25) * mm, "end": v(0, 104.25) * mm, "construction": true});
            skArc(sketch, "E80", {"start": v(15, 104.25) * mm, "mid": v(0, 119.25) * mm, "end": v(-15, 104.25) * mm});
            skLineSegment(sketch, "E81", {"start": v(15, 104.25) * mm, "end": v(15, 92.25) * mm});
            skLineSegment(sketch, "E82", {"start": v(-15, 104.25) * mm, "end": v(-15, 92.25) * mm});
            skLineSegment(sketch, "E83", {"start": v(15, 92.25) * mm, "end": v(33, 74.25) * mm});
            skLineSegment(sketch, "E84", {"start": v(-15, 92.25) * mm, "end": v(-33, 74.25) * mm});
            skCircle(sketch, "E85", {"center": v(0, 104.25) * mm, "radius": 6 * mm});
            skLineSegment(sketch, "E86", {"start": v(4.2, -74.25) * mm, "end": v(4.2, -104.25) * mm, "construction": true});
            skArc(sketch, "E87", {"start": v(-10.8, -104.25) * mm, "mid": v(4.2, -119.25) * mm, "end": v(19.2, -104.25) * mm});
            skLineSegment(sketch, "E88", {"start": v(-10.8, -104.25) * mm, "end": v(-10.8, -92.25) * mm});
            skLineSegment(sketch, "E89", {"start": v(19.2, -104.25) * mm, "end": v(19.2, -92.25) * mm});
            skLineSegment(sketch, "E90", {"start": v(-10.8, -92.25) * mm, "end": v(-28.8, -74.25) * mm});
            skLineSegment(sketch, "E91", {"start": v(19.2, -92.25) * mm, "end": v(37.2, -74.25) * mm});
            skCircle(sketch, "E92", {"center": v(4.2, -104.25) * mm, "radius": 6 * mm});
            skSolve(sketch);
        }
        {
            var Q0;
            Q0=makeQuery(id+"F16.imprint","IMPRINT",FACE,{"disambiguationData":[TD([[makeQuery(id+"F16.imprint","IMPRINT",EDGE,{"derivedFrom":sQuery(id+"F16.wireOp",EDGE,"E80")}),1.0]])]});
            var Q1;
            Q1=makeQuery(id+"F16.imprint","IMPRINT",FACE,{"disambiguationData":[TD([[makeQuery(id+"F16.imprint","IMPRINT",EDGE,{"derivedFrom":sQuery(id+"F16.wireOp",EDGE,"E87")}),1.0]])]});
            var Q2;
            Q2=makeQuery(id+"F16.imprint","IMPRINT",FACE,{"disambiguationData":[TD([[makeQuery(id+"F16.imprint","IMPRINT",EDGE,{"derivedFrom":makeQuery(id+"F1.opExtrude","CAP_EDGE",EDGE,{"disambiguationData":[OSD([sQuery(id+"F0.wireOp",EDGE,"E1.left")])],"isStart":true})}),-1.0]])]});
            var Q3;
            Q3=makeQuery(id+"F2.opExtrude","CAP_FACE",FACE,{"disambiguationData":[OSD([sQuery(id+"F0.wireOp",EDGE,"E12"),sQuery(id+"F0.wireOp",EDGE,"E13"),sQuery(id+"F0.wireOp",EDGE,"E14"),sQuery(id+"F0.wireOp",EDGE,"E15"),sQuery(id+"F0.wireOp",EDGE,"E17.filletArc"),sQuery(id+"F0.wireOp",EDGE,"E18.filletArc"),sQuery(id+"F0.wireOp",EDGE,"E19.filletArc"),sQuery(id+"F0.wireOp",EDGE,"E20.filletArc"),sQuery(id+"F0.wireOp",EDGE,"E25.0"),sQuery(id+"F0.wireOp",EDGE,"E25.1"),sQuery(id+"F0.wireOp",EDGE,"E25.2"),sQuery(id+"F0.wireOp",EDGE,"E25.3"),sQuery(id+"F0.wireOp",EDGE,"E25.4"),sQuery(id+"F0.wireOp",EDGE,"E25.5"),sQuery(id+"F0.wireOp",EDGE,"E25.6"),sQuery(id+"F0.wireOp",EDGE,"E25.7")])],"isStart":false});
            extrude(context, id + "F17", {"entities" : qUnion([Q0, Q1, Q2]), "endBound" : BoundingType.UP_TO_SURFACE, "endBoundEntityFace" : qUnion([Q3]), "depth" : 3 * mm});
        }
    });
